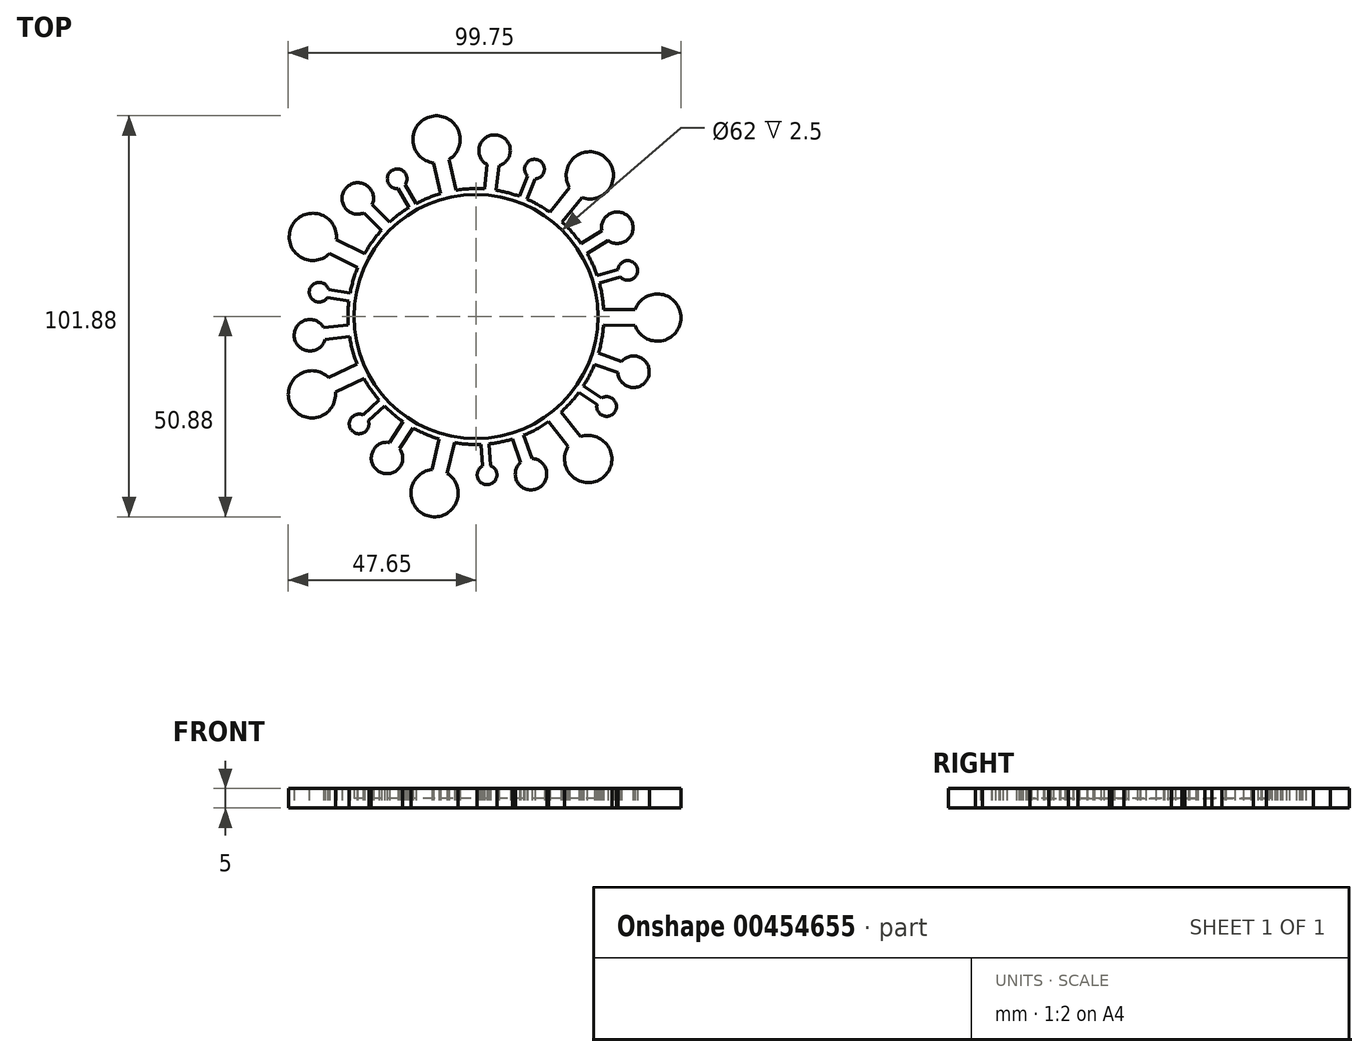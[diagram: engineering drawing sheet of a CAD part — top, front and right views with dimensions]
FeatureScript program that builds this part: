
annotation { "Feature Type Name" : "Feature", "Feature Type Description" : "" }
export const myFeature = defineFeature(function(context is Context, id is Id, definition is map)
    precondition{}
    {
        {
            var Q0;
            Q0=qCreatedBy(makeId("Top.planeOp"),FACE);
            var sketch = newSketch(context, id + "F0", { "sketchPlane" : qUnion([Q0])});
            skCircle(sketch, "E0", {"center": v(0, 0) * mm, "radius": 31 * mm});
            skCircle(sketch, "E1", {"center": v(0, 0) * mm, "radius": 32.5 * mm});
            skCircle(sketch, "E2", {"center": v(-30, 30) * mm, "radius": 4 * mm});
            skCircle(sketch, "E3", {"center": v(-20, 35) * mm, "radius": 2.5 * mm});
            skCircle(sketch, "E4", {"center": v(-10, 45) * mm, "radius": 6 * mm});
            skLineSegment(sketch, "E5", {"start": v(0, 0) * mm, "end": v(-22.98, 22.98) * mm, "construction": true});
            skLineSegment(sketch, "E6", {"start": v(0, 0) * mm, "end": v(-16.12, 28.22) * mm, "construction": true});
            skLineSegment(sketch, "E7", {"start": v(0, 0) * mm, "end": v(-7.05, 31.73) * mm, "construction": true});
            skLineSegment(sketch, "E8", {"start": v(-22.98, 22.98) * mm, "end": v(-22.98, 22.98) * mm});
            skLineSegment(sketch, "E9", {"start": v(-20, 35) * mm, "end": v(-18.76, 32.83) * mm});
            skLineSegment(sketch, "E10", {"start": v(-10, 45) * mm, "end": v(-8.7, 39.14) * mm});
            skLineSegment(sketch, "E11.0", {"start": v(-5.08, 32.1) * mm, "end": v(-6.82, 39.91) * mm});
            skPoint(sketch, "E12", {"position": v(-28.44, 26.32) * mm});
            skPoint(sketch, "E13", {"position": v(-26.32, 28.44) * mm});
            skPoint(sketch, "E14", {"position": v(-24.02, 21.9) * mm});
            skPoint(sketch, "E15", {"position": v(-21.9, 24.02) * mm});
            skPoint(sketch, "E16", {"position": v(-16.99, 27.7) * mm});
            skPoint(sketch, "E17", {"position": v(-15.25, 28.7) * mm});
            skPoint(sketch, "E18", {"position": v(-19.73, 32.51) * mm});
            skPoint(sketch, "E19", {"position": v(-18, 33.5) * mm});
            skPoint(sketch, "E20", {"position": v(-8.99, 31.23) * mm});
            skPoint(sketch, "E21", {"position": v(-5.08, 32.1) * mm});
            skPoint(sketch, "E22", {"position": v(-10.73, 39.04) * mm});
            skPoint(sketch, "E23", {"position": v(-6.82, 39.91) * mm});
            skLineSegment(sketch, "E24.trimOffspring", {"start": v(-24.02, 21.9) * mm, "end": v(-28.44, 26.32) * mm});
            skLineSegment(sketch, "E25.trimOffspring", {"start": v(-21.9, 24.02) * mm, "end": v(-26.32, 28.44) * mm});
            skLineSegment(sketch, "E26.trimOffspring", {"start": v(-16.99, 27.7) * mm, "end": v(-19.73, 32.51) * mm});
            skLineSegment(sketch, "E27.trimOffspring", {"start": v(-15.25, 28.7) * mm, "end": v(-18, 33.5) * mm});
            skLineSegment(sketch, "E28.trimOffspring", {"start": v(-18.76, 32.83) * mm, "end": v(-20, 35) * mm, "construction": true});
            skLineSegment(sketch, "E29.trimOffspring", {"start": v(-8.99, 31.23) * mm, "end": v(-10.73, 39.04) * mm});
            skCircle(sketch, "E30.1.0", {"center": v(-41.42, 20.24) * mm, "radius": 6 * mm});
            skLineSegment(sketch, "E30.1.1", {"start": v(-28.27, 16.04) * mm, "end": v(-35.46, 19.55) * mm});
            skLineSegment(sketch, "E30.1.2", {"start": v(-30.02, 12.44) * mm, "end": v(-37.21, 15.96) * mm});
            skCircle(sketch, "E30.2.0", {"center": v(-41.65, -19.76) * mm, "radius": 6 * mm});
            skLineSegment(sketch, "E30.2.1", {"start": v(-30.16, -12.1) * mm, "end": v(-37.4, -15.53) * mm});
            skLineSegment(sketch, "E30.2.2", {"start": v(-28.45, -15.71) * mm, "end": v(-35.68, -19.14) * mm});
            skCircle(sketch, "E30.3.0", {"center": v(-10.52, -44.88) * mm, "radius": 6 * mm});
            skLineSegment(sketch, "E30.3.1", {"start": v(-9.35, -31.13) * mm, "end": v(-11.17, -38.92) * mm});
            skLineSegment(sketch, "E30.3.2", {"start": v(-5.45, -32.04) * mm, "end": v(-7.28, -39.83) * mm});
            skCircle(sketch, "E30.4.0", {"center": v(28.53, -36.2) * mm, "radius": 6 * mm});
            skLineSegment(sketch, "E30.4.1", {"start": v(18.5, -26.71) * mm, "end": v(23.46, -33) * mm});
            skLineSegment(sketch, "E30.4.2", {"start": v(21.65, -24.24) * mm, "end": v(26.6, -30.52) * mm});
            skCircle(sketch, "E30.5.0", {"center": v(46.1, -0.26) * mm, "radius": 6 * mm});
            skLineSegment(sketch, "E30.5.1", {"start": v(32.43, -2.19) * mm, "end": v(40.43, -2.23) * mm});
            skLineSegment(sketch, "E30.5.2", {"start": v(32.45, 1.81) * mm, "end": v(40.45, 1.77) * mm});
            skCircle(sketch, "E30.6.0", {"center": v(28.95, 35.88) * mm, "radius": 6 * mm});
            skLineSegment(sketch, "E30.6.1", {"start": v(21.93, 23.99) * mm, "end": v(26.95, 30.22) * mm});
            skLineSegment(sketch, "E30.6.2", {"start": v(18.81, 26.5) * mm, "end": v(23.84, 32.73) * mm});
            skCircle(sketch, "E31.1.0", {"center": v(-39.83, 6.19) * mm, "radius": 2.5 * mm});
            skLineSegment(sketch, "E31.1.1", {"start": v(-31.95, 5.97) * mm, "end": v(-37.42, 6.82) * mm});
            skLineSegment(sketch, "E31.1.2", {"start": v(-32.25, 4) * mm, "end": v(-37.72, 4.85) * mm});
            skCircle(sketch, "E31.2.0", {"center": v(-29.67, -27.29) * mm, "radius": 2.5 * mm});
            skLineSegment(sketch, "E31.2.1", {"start": v(-24.59, -21.25) * mm, "end": v(-28.66, -25) * mm});
            skLineSegment(sketch, "E31.2.2", {"start": v(-23.23, -22.72) * mm, "end": v(-27.3, -26.47) * mm});
            skCircle(sketch, "E31.3.0", {"center": v(2.83, -40.21) * mm, "radius": 2.5 * mm});
            skLineSegment(sketch, "E31.3.1", {"start": v(1.29, -32.47) * mm, "end": v(1.67, -38) * mm});
            skLineSegment(sketch, "E31.3.2", {"start": v(3.28, -32.33) * mm, "end": v(3.67, -37.86) * mm});
            skCircle(sketch, "E31.4.0", {"center": v(33.2, -22.86) * mm, "radius": 2.5 * mm});
            skLineSegment(sketch, "E31.4.1", {"start": v(26.2, -19.24) * mm, "end": v(30.75, -22.38) * mm});
            skLineSegment(sketch, "E31.4.2", {"start": v(27.33, -17.6) * mm, "end": v(31.88, -20.73) * mm});
            skCircle(sketch, "E31.5.0", {"center": v(38.57, 11.71) * mm, "radius": 2.5 * mm});
            skLineSegment(sketch, "E31.5.1", {"start": v(31.37, 8.48) * mm, "end": v(36.67, 10.09) * mm});
            skLineSegment(sketch, "E31.5.2", {"start": v(30.8, 10.4) * mm, "end": v(36.09, 12) * mm});
            skCircle(sketch, "E31.6.0", {"center": v(14.9, 37.46) * mm, "radius": 2.5 * mm});
            skLineSegment(sketch, "E31.6.1", {"start": v(12.93, 29.82) * mm, "end": v(14.98, 34.96) * mm});
            skLineSegment(sketch, "E31.6.2", {"start": v(11.07, 30.56) * mm, "end": v(13.12, 35.7) * mm});
            skCircle(sketch, "E32.1.0", {"center": v(-42.16, -4.75) * mm, "radius": 4 * mm});
            skLineSegment(sketch, "E32.1.1", {"start": v(-32.43, -2.14) * mm, "end": v(-38.64, -2.84) * mm});
            skLineSegment(sketch, "E32.1.2", {"start": v(-32.1, -5.13) * mm, "end": v(-38.3, -5.83) * mm});
            skCircle(sketch, "E32.2.0", {"center": v(-22.57, -35.92) * mm, "radius": 4 * mm});
            skLineSegment(sketch, "E32.2.1", {"start": v(-18.54, -26.7) * mm, "end": v(-21.87, -31.99) * mm});
            skLineSegment(sketch, "E32.2.2", {"start": v(-16, -28.29) * mm, "end": v(-19.33, -33.58) * mm});
            skCircle(sketch, "E32.3.0", {"center": v(14.01, -40.05) * mm, "radius": 4 * mm});
            skLineSegment(sketch, "E32.3.1", {"start": v(9.3, -31.14) * mm, "end": v(11.37, -37.04) * mm});
            skLineSegment(sketch, "E32.3.2", {"start": v(12.14, -30.15) * mm, "end": v(14.2, -36.05) * mm});
            skCircle(sketch, "E32.4.0", {"center": v(40.05, -14.01) * mm, "radius": 4 * mm});
            skLineSegment(sketch, "E32.4.1", {"start": v(30.15, -12.14) * mm, "end": v(36.05, -14.2) * mm});
            skLineSegment(sketch, "E32.4.2", {"start": v(31.14, -9.3) * mm, "end": v(37.04, -11.37) * mm});
            skCircle(sketch, "E32.5.0", {"center": v(35.92, 22.57) * mm, "radius": 4 * mm});
            skLineSegment(sketch, "E32.5.1", {"start": v(28.29, 16) * mm, "end": v(33.58, 19.33) * mm});
            skLineSegment(sketch, "E32.5.2", {"start": v(26.7, 18.54) * mm, "end": v(31.99, 21.87) * mm});
            skCircle(sketch, "E32.6.0", {"center": v(4.75, 42.16) * mm, "radius": 4 * mm});
            skLineSegment(sketch, "E32.6.1", {"start": v(5.13, 32.1) * mm, "end": v(5.83, 38.3) * mm});
            skLineSegment(sketch, "E32.6.2", {"start": v(2.14, 32.43) * mm, "end": v(2.84, 38.64) * mm});
            skSolve(sketch);
        }
        {
            var Q0;
            Q0 = qSketchRegion(id + "F0", true);
            extrude(context, id + "F1", {"entities" : qUnion([Q0]), "depth" : 5 * mm});
        }
        {
            var Q0;
            Q0=makeQuery(id+"F0.imprint","IMPRINT",FACE,{"disambiguationData":[TD([[makeQuery(id+"F0.imprint","IMPRINT",EDGE,{"derivedFrom":sQuery(id+"F0.wireOp",EDGE,"E0")}),1.0]])]});
            var Q1;
            {var subQ0=sQuery(id+"F0.wireOp",EDGE,"1ae0b59a-bd55-4602-b89c-cc70d0e80a3e.0");var subQ1=sQuery(id+"F0.wireOp",EDGE,"a143d85c-ea0c-4c31-83c6-3a43c6711e3a.0");var subQ2=makeQuery(id+"F0.imprint","INTERSECT",VERTEX,{"derivedFrom":[subQ1,subQ0]});Q1=makeQuery(id+"F0.imprint","IMPRINT",FACE,{"disambiguationData":[TD([[makeQuery(id+"F0.imprint","IMPRINT",EDGE,{"disambiguationData":[TD([[subQ2,-1.0]])],"derivedFrom":subQ1}),-1.0]])]});}
            extrude(context, id + "F2", {"entities" : qUnion([Q0, Q1]), "operationType" : NewBodyOperationType.ADD, "depth" : 2.5 * mm});
        }
    });
